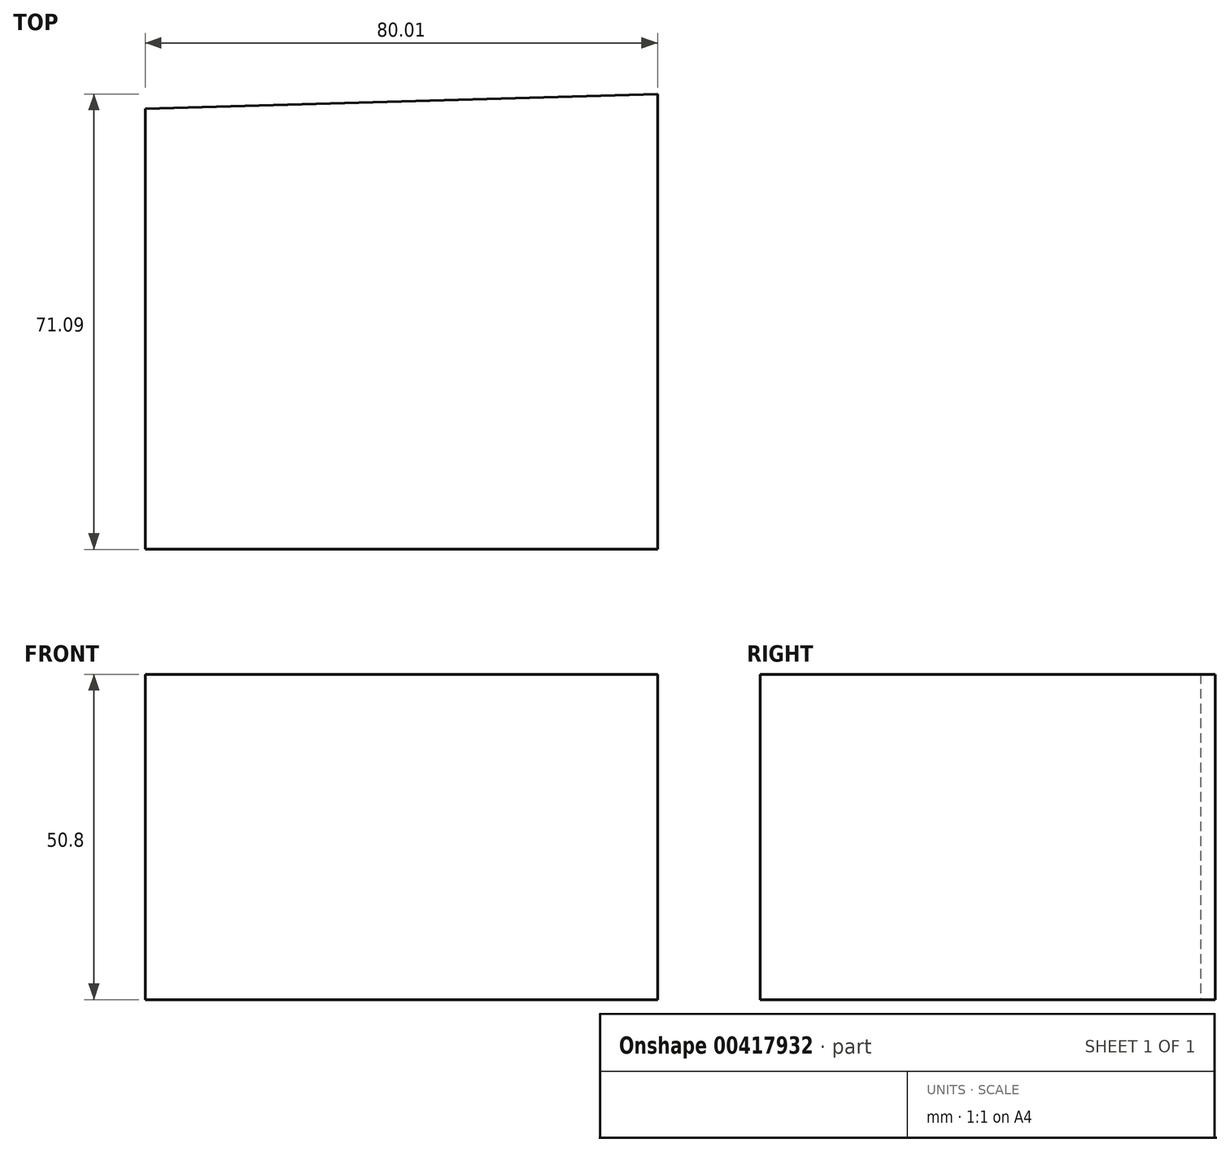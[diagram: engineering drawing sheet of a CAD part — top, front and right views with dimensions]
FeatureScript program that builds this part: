
annotation { "Feature Type Name" : "Feature", "Feature Type Description" : "" }
export const myFeature = defineFeature(function(context is Context, id is Id, definition is map)
    precondition{}
    {
        {
            var Q0;
            Q0=qCreatedBy(makeId("Top.planeOp"),FACE);
            var sketch = newSketch(context, id + "F0", { "sketchPlane" : qUnion([Q0])});
            skLineSegment(sketch, "E0", {"start": v(-38.57, 28.78) * mm, "end": v(-38.57, -40) * mm});
            skLineSegment(sketch, "E1", {"start": v(-38.57, -40) * mm, "end": v(41.44, -40) * mm});
            skLineSegment(sketch, "E2", {"start": v(41.44, -40) * mm, "end": v(41.44, 31.08) * mm});
            skLineSegment(sketch, "E3", {"start": v(41.44, 31.08) * mm, "end": v(-38.57, 28.78) * mm});
            skSolve(sketch);
        }
        {
            var Q0;
            Q0 = qSketchRegion(id + "F0", true);
            extrude(context, id + "F1", {"entities" : qUnion([Q0]), "depth" : 50.8 * mm});
        }
    });
